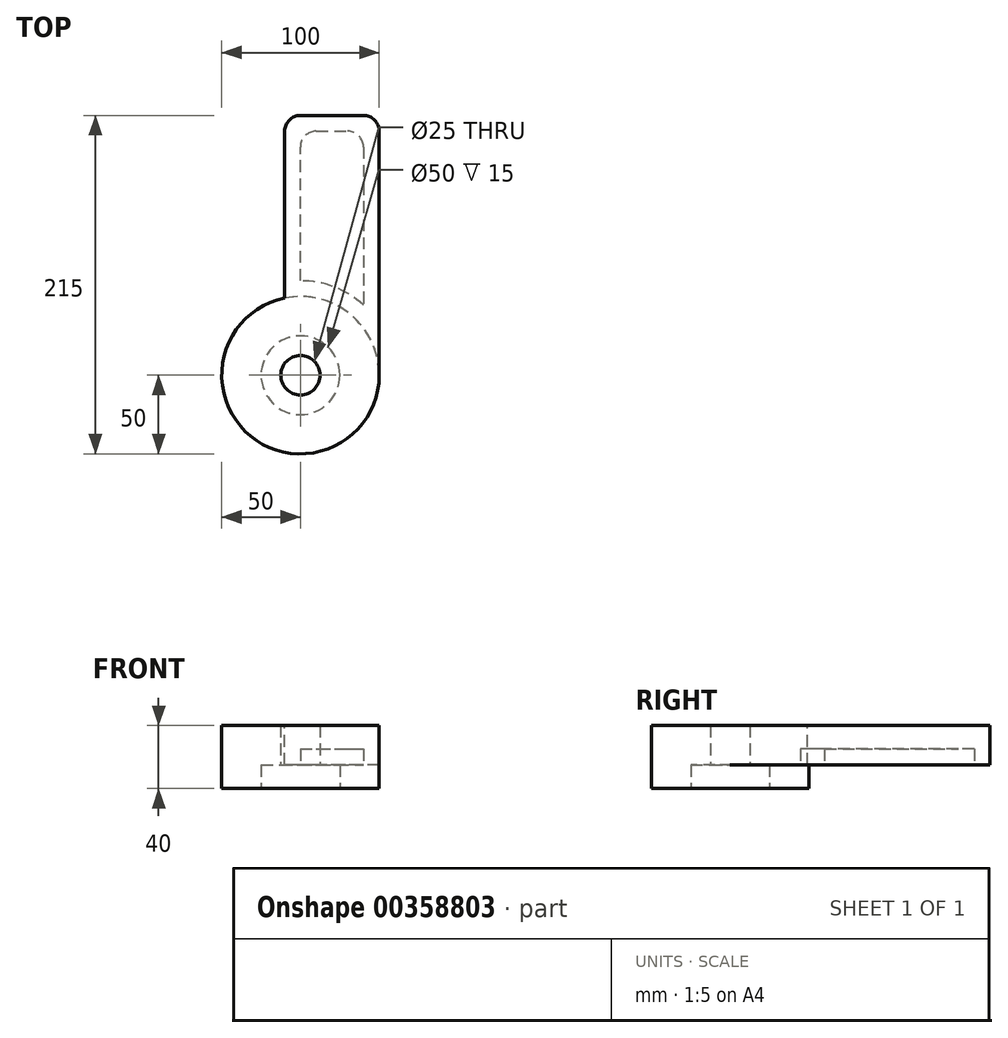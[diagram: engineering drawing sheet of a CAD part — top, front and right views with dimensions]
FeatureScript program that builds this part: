
annotation { "Feature Type Name" : "Feature", "Feature Type Description" : "" }
export const myFeature = defineFeature(function(context is Context, id is Id, definition is map)
    precondition{}
    {
        {
            var Q0;
            Q0=qCreatedBy(makeId("Top.planeOp"),FACE);
            var sketch = newSketch(context, id + "F0", { "sketchPlane" : qUnion([Q0])});
            skCircle(sketch, "E0", {"center": v(0, 0) * mm, "radius": 50 * mm});
            skLineSegment(sketch, "E1.bottom", {"start": v(50, 0) * mm, "end": v(-10, 0) * mm});
            skLineSegment(sketch, "E1.top", {"start": v(50, 165) * mm, "end": v(-10, 165) * mm});
            skLineSegment(sketch, "E1.left", {"start": v(50, 0) * mm, "end": v(50, 165) * mm});
            skLineSegment(sketch, "E1.right", {"start": v(-10, 0) * mm, "end": v(-10, 165) * mm});
            skSolve(sketch);
        }
        {
            var Q0;
            {var subQ4=sQuery(id+"F0.wireOp",EDGE,"E1.top");Q0=makeQuery(id+"F0.imprint","IMPRINT",FACE,{"disambiguationData":[TD([[makeQuery(id+"F0.imprint","IMPRINT",EDGE,{"derivedFrom":subQ4}),1.0]])]});}
            extrude(context, id + "F1", {"entities" : qUnion([Q0]), "oppositeDirection" : true, "depth" : 25 * mm});
        }
        {
            var Q0;
            {var subQ0=sQuery(id+"F0.wireOp",EDGE,"E1.bottom");Q0=makeQuery(id+"F0.imprint","IMPRINT",FACE,{"disambiguationData":[TD([[makeQuery(id+"F0.imprint","IMPRINT",EDGE,{"derivedFrom":subQ0}),-1.0]])]});}
            var Q1;
            {var subQ0=sQuery(id+"F0.wireOp",EDGE,"E1.bottom");Q1=makeQuery(id+"F0.imprint","IMPRINT",FACE,{"disambiguationData":[TD([[makeQuery(id+"F0.imprint","IMPRINT",EDGE,{"derivedFrom":subQ0}),1.0]])]});}
            extrude(context, id + "F2", {"entities" : qUnion([Q0, Q1]), "operationType" : NewBodyOperationType.ADD, "oppositeDirection" : true, "depth" : 40 * mm});
        }
        {
            var Q0;
            Q0=makeQuery(id+"F2.opExtrude","CAP_FACE",FACE,{"disambiguationData":[OSD([sQuery(id+"F0.wireOp",EDGE,"E0")])],"isStart":false});
            var sketch = newSketch(context, id + "F3", { "sketchPlane" : qUnion([Q0])});
            skCircle(sketch, "E2", {"center": v(0, 0) * mm, "radius": 12.5 * mm});
            skSolve(sketch);
        }
        {
            var Q0;
            Q0 = qSketchRegion(id + "F3", true);
            extrude(context, id + "F4", {"entities" : qUnion([Q0]), "operationType" : NewBodyOperationType.REMOVE, "endBound" : BoundingType.THROUGH_ALL, "oppositeDirection" : true, "depth" : 25 * mm});
        }
        {
            var Q0;
            Q0=makeQuery(id+"F2.opExtrude","CAP_FACE",FACE,{"disambiguationData":[OSD([sQuery(id+"F0.wireOp",EDGE,"E0")])],"isStart":false});
            var sketch = newSketch(context, id + "F5", { "sketchPlane" : qUnion([Q0])});
            skCircle(sketch, "E3", {"center": v(0, 0) * mm, "radius": 25 * mm});
            skSolve(sketch);
        }
        {
            var Q0;
            Q0 = qSketchRegion(id + "F5", true);
            extrude(context, id + "F6", {"entities" : qUnion([Q0]), "operationType" : NewBodyOperationType.REMOVE, "oppositeDirection" : true, "depth" : 15 * mm});
        }
        {
            var Q0;
            Q0=makeQuery(id+"F1.opExtrude","SWEPT_EDGE",EDGE,{"disambiguationData":[OSD([sQuery(id+"F0.wireOp",EDGE,"E1.top"),sQuery(id+"F0.wireOp",EDGE,"E1.right")])]});
            var Q1;
            Q1=makeQuery(id+"F1.opExtrude","SWEPT_EDGE",EDGE,{"disambiguationData":[OSD([sQuery(id+"F0.wireOp",EDGE,"E1.top"),sQuery(id+"F0.wireOp",EDGE,"E1.left")])]});
            fillet(context, id + "F7", {"entities" : qUnion([Q0, Q1]), "radius" : 10 * mm, "tangentPropagation" : true, "allowEdgeOverflow" : false});
        }
        {
            var Q0;
            Q0=makeQuery(id+"F1.opExtrude","CAP_FACE",FACE,{"disambiguationData":[OSD([sQuery(id+"F0.wireOp",EDGE,"E0"),sQuery(id+"F0.wireOp",EDGE,"E1.top"),sQuery(id+"F0.wireOp",EDGE,"E1.left"),sQuery(id+"F0.wireOp",EDGE,"E1.right")])],"isStart":false});
            var sketch = newSketch(context, id + "F8", { "sketchPlane" : qUnion([Q0])});
            skLineSegment(sketch, "E4.0", {"start": v(0, -155) * mm, "end": v(0, -155) * mm});
            skLineSegment(sketch, "E4.1", {"start": v(40, -155) * mm, "end": v(40, -155) * mm});
            skLineSegment(sketch, "E4.2", {"start": v(40, -155) * mm, "end": v(40, -44.72) * mm});
            skLineSegment(sketch, "E4.3", {"start": v(0, -155) * mm, "end": v(40, -155) * mm});
            skArc(sketch, "E4.4", {"start": v(40, -44.72) * mm, "mid": v(21.4, -56.05) * mm, "end": v(0, -60) * mm});
            skLineSegment(sketch, "E4.5", {"start": v(0, -60) * mm, "end": v(0, -155) * mm});
            skSolve(sketch);
        }
        {
            var Q0;
            Q0 = qSketchRegion(id + "F8", true);
            extrude(context, id + "F9", {"entities" : qUnion([Q0]), "operationType" : NewBodyOperationType.REMOVE, "oppositeDirection" : true, "depth" : 10 * mm});
        }
        {
            var Q0;
            Q0=makeQuery(id+"F9.boolean.opBoolean","COPY",EDGE,{"derivedFrom":makeQuery(id+"F9.opExtrude","SWEPT_EDGE",EDGE,{"disambiguationData":[OSD([sQuery(id+"F8.wireOp",EDGE,"E4.3"),sQuery(id+"F8.wireOp",EDGE,"E4.5")])]})});
            var Q1;
            Q1=makeQuery(id+"F9.boolean.opBoolean","COPY",EDGE,{"derivedFrom":makeQuery(id+"F9.opExtrude","SWEPT_EDGE",EDGE,{"disambiguationData":[OSD([sQuery(id+"F8.wireOp",EDGE,"E4.2"),sQuery(id+"F8.wireOp",EDGE,"E4.3")])]})});
            fillet(context, id + "F10", {"entities" : qUnion([Q0, Q1]), "radius" : 10 * mm, "tangentPropagation" : true, "allowEdgeOverflow" : false});
        }
    });
